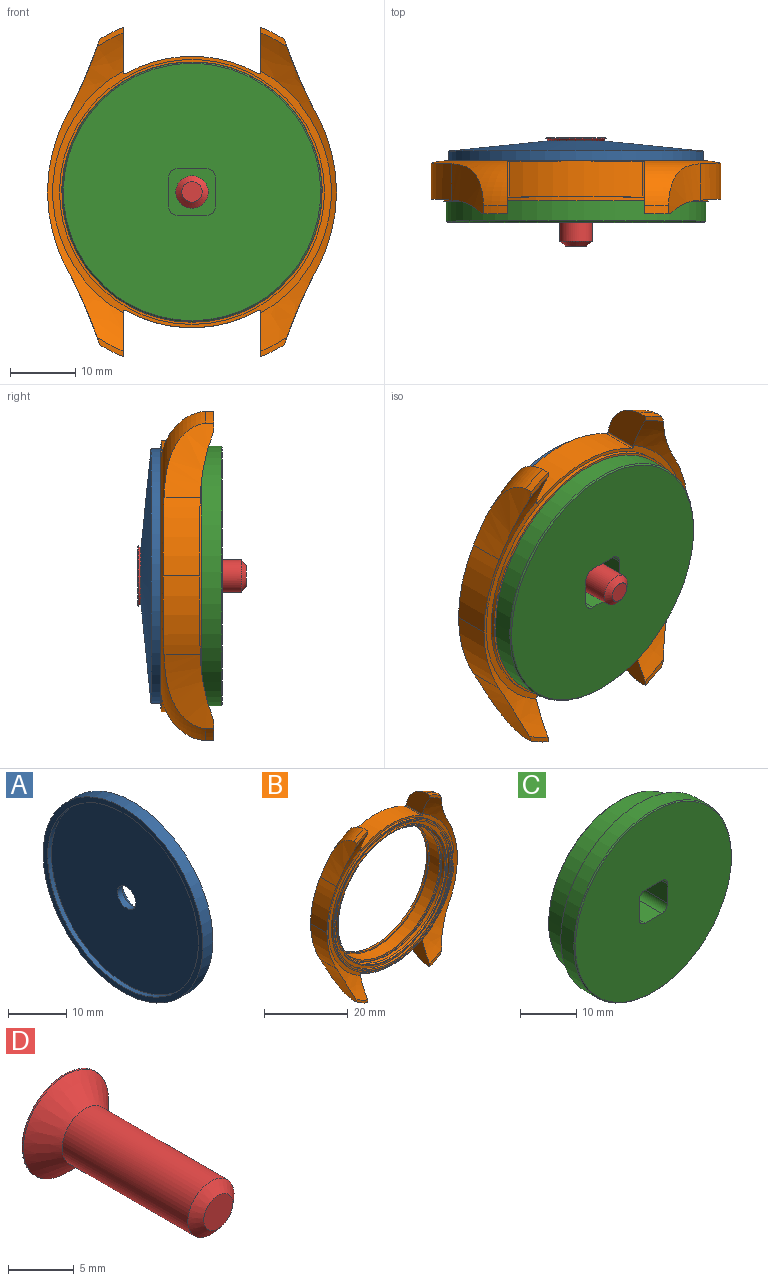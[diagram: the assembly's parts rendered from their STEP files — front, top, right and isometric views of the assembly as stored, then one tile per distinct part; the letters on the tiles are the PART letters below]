
ASSEMBLY  parts=4 mates=3
PART A: 7 faces, bbox 4x38.9x38.9 mm
  f0: cone r=19.47mm half-angle=84.2deg, axis (-1,0,0), area 1141.1mm2, adj f1,f6
  f1: cylinder r=19.47mm len=38.95mm, axis (-1,0,0), area 297.3mm2, adj f0,f2
  f2: plane 38.95x38.95mm, normal (-1,0,0), area 130.5mm2, adj f1,f3
  f3: cylinder r=18.38mm len=36.75mm, axis (-1,0,0), area 107.4mm2, adj f2,f4
  f4: plane 36.75x36.75mm, normal (-1,0,0), area 1044.8mm2, adj f3,f5
  f5: cylinder r=2.25mm len=4.5mm, axis (-1,0,0), area 17.6mm2, adj f4,f6
  f6: bspline ~8.47x8.47mm, area 54.6mm2, adj f0,f5
PART B: 54 faces, bbox 59.5x8.5x59.5 mm
  f0: cylinder r=27.3mm len=3.62mm, axis (0,-1,0), area 5mm2, adj f6,f9,f38,f49
  f1: cylinder r=27.3mm len=3.62mm, axis (0,-1,0), area 5mm2, adj f9,f35,f41,f45
  f2: plane 4x2.97mm, normal (0,-1,0), area 3.3mm2, adj f5,f7,f39,f48
  f3: plane 4x2.97mm, normal (0,-1,0), area 3.3mm2, adj f8,f34,f36,f44
  f4: plane 42.6x41.5mm, normal (0,-1,0), area 113mm2, adj f5,f33,f34,f36,f37,f38,f39,f40
  f5: torus R=10.97mm, axis (0,-1,0), area 112mm2, adj f2,f4,f6,f38,f39,f46,f47,f48
  f6: plane 4x2.97mm, normal (0,-1,0), area 3.3mm2, adj f0,f5,f38,f49
  f7: cylinder r=27.3mm len=3.62mm, axis (0,-1,0), area 5mm2, adj f2,f9,f39,f48
  f8: cylinder r=27.3mm len=3.62mm, axis (0,-1,0), area 5mm2, adj f3,f9,f36,f44
  f9: torus R=19.83mm, axis (0,-1,0), area 415.4mm2, adj f0,f1,f7,f8,f10,f36,f37,f38
  f10: plane 40.38x40.38mm, normal (0,1,0), area 90.5mm2, adj f9,f11
  f11: cylinder r=19.46mm len=38.93mm, axis (0,-1,0), area 137.6mm2, adj f10,f12
  f12: plane 38.93x38.93mm, normal (0,1,0), area 92.9mm2, adj f11,f13
  f13: cylinder r=18.69mm len=37.38mm, axis (0,-1,0), area 23.5mm2, adj f12,f14
  f14: plane 37.38x37.38mm, normal (0,1,0), area 49.2mm2, adj f13,f15
  f15: cone r=18.35mm half-angle=30deg, axis (0,1,0), area 19.9mm2, adj f14,f16
  f16: cylinder r=18.35mm len=36.7mm, axis (0,-1,0), area 89.4mm2, adj f15,f17
  f17: plane 36.7x36.7mm, normal (0,1,0), area 94.9mm2, adj f16,f18
  f18: cylinder r=17.51mm len=35.02mm, axis (0,-1,0), area 66mm2, adj f17,f19
  f19: plane 35.72x35.72mm, normal (0,-1,0), area 38.9mm2, adj f18,f20
  f20: cylinder r=17.86mm len=35.72mm, axis (0,-1,0), area 387.1mm2, adj f19,f21
  f21: plane 36.6x36.6mm, normal (0,-1,0), area 50.3mm2, adj f20,f22
  f22: cylinder r=18.3mm len=36.6mm, axis (0,-1,0), area 34.5mm2, adj f21,f23
  f23: cone r=18.3mm half-angle=43.3deg, axis (0,1,0), area 47.9mm2, adj f22,f24
  f24: cylinder r=18.01mm len=36.03mm, axis (0,-1,0), area 100.6mm2, adj f23,f25
  f25: cone r=18.3mm half-angle=43.3deg, axis (0,-1,0), area 47.9mm2, adj f24,f26
  f26: plane 37.03x37.03mm, normal (0,-1,0), area 24.6mm2, adj f25,f27
  f27: cylinder r=18.51mm len=37.03mm, axis (0,-1,0), area 65.7mm2, adj f26,f28
  f28: plane 39x39mm, normal (0,-1,0), area 117.6mm2, adj f27,f29
  f29: cylinder r=19.5mm len=39mm, axis (0,-1,0), area 75.3mm2, adj f28,f30
  f30: plane 39.83x39.83mm, normal (0,-1,0), area 51.4mm2, adj f29,f31
  f31: cylinder r=19.91mm len=39.83mm, axis (0,-1,0), area 31.3mm2, adj f30,f32
  f32: plane 40.5x40.5mm, normal (0,-1,0), area 42.6mm2, adj f31,f33
  f33: cylinder r=20.25mm len=40.5mm, axis (0,-1,0), area 76.3mm2, adj f4,f32
  f34: torus R=10.97mm, axis (0,-1,0), area 112mm2, adj f3,f4,f35,f36,f41,f42,f43,f44
  f35: plane 4x2.97mm, normal (0,-1,0), area 3.3mm2, adj f1,f34,f41,f45
  f36: plane 8.38x7.32mm, normal (-1,0,0), area 34.6mm2, adj f3,f4,f8,f9,f34,f50
  f37: cylinder r=20.75mm len=20.4mm, axis (0,1,0), area 117.4mm2, adj f4,f9,f50,f51
  f38: plane 8.38x7.32mm, normal (1,0,0), area 34.6mm2, adj f0,f4,f5,f6,f9,f51
  f39: plane 8.38x7.32mm, normal (1,0,0), area 34.6mm2, adj f2,f4,f5,f7,f9,f53
  f40: cylinder r=20.75mm len=20.4mm, axis (0,1,0), area 117.4mm2, adj f4,f9,f52,f53
  f41: plane 8.38x7.32mm, normal (-1,0,0), area 34.6mm2, adj f1,f4,f9,f34,f35,f52
  f42: cylinder r=25.39mm len=12.04mm, axis (0,1,0), area 69.5mm2, adj f9,f34,f43,f45
  f43: cylinder r=25.39mm len=12.04mm, axis (0,1,0), area 69.5mm2, adj f9,f34,f42,f44
  f44: cylinder r=67.35mm len=11.33mm, axis (0,1,0), area 62.4mm2, adj f3,f8,f9,f34,f43
  f45: cylinder r=67.35mm len=11.33mm, axis (0,1,0), area 62.4mm2, adj f1,f9,f34,f35,f42
  f46: cylinder r=25.39mm len=12.04mm, axis (0,1,0), area 69.5mm2, adj f5,f9,f47,f49
  f47: cylinder r=25.39mm len=12.04mm, axis (0,1,0), area 69.5mm2, adj f5,f9,f46,f48
  f48: cylinder r=67.35mm len=11.33mm, axis (0,1,0), area 62.4mm2, adj f2,f5,f7,f9,f47
  f49: cylinder r=67.35mm len=11.33mm, axis (0,1,0), area 62.4mm2, adj f0,f5,f6,f9,f46
  f50: cylinder r=0.2mm len=5.5mm, axis (0,1,0), area 2.3mm2, adj f4,f9,f36,f37
  f51: cylinder r=0.2mm len=5.5mm, axis (0,1,0), area 2.3mm2, adj f4,f9,f37,f38
  f52: cylinder r=0.2mm len=5.5mm, axis (0,1,0), area 2.3mm2, adj f4,f9,f40,f41
  f53: cylinder r=0.2mm len=5.5mm, axis (0,1,0), area 2.3mm2, adj f4,f9,f39,f40
PART C: 17 faces, bbox 39.8x8.8x39.8 mm
  f0: plane 39.35x39.35mm, normal (0,-1,0), area 1166.2mm2, adj f6,f7,f8,f9,f10,f11,f12,f13
  f1: cylinder r=2.25mm len=4.5mm, axis (0,1,0), area 25.4mm2, adj f4,f14
  f2: plane 39.75x39.75mm, normal (0,1,0), area 242.8mm2, adj f3,f5
  f3: cylinder r=17.82mm len=35.65mm, axis (0,-1,0), area 571.2mm2, adj f2,f15
  f4: plane 35.25x35.25mm, normal (0,1,0), area 960mm2, adj f1,f15
  f5: cylinder r=19.88mm len=39.75mm, axis (0,-1,0), area 412.1mm2, adj f2,f16
  f6: plane 7x4.2mm, normal (0,0,1), area 29.4mm2, adj f0,f7,f13,f14
  f7: cylinder r=1.5mm len=7mm, axis (0,-1,0), area 16.5mm2, adj f0,f6,f8,f14
  f8: plane 7x4.2mm, normal (-1,0,0), area 29.4mm2, adj f0,f7,f9,f14
  f9: cylinder r=1.5mm len=7mm, axis (0,-1,0), area 16.5mm2, adj f0,f8,f10,f14
  f10: plane 7x4.2mm, normal (0,0,-1), area 29.4mm2, adj f0,f9,f11,f14
  f11: cylinder r=1.5mm len=7mm, axis (0,-1,0), area 16.5mm2, adj f0,f10,f12,f14
  f12: plane 7x4.2mm, normal (1,0,0), area 29.4mm2, adj f0,f11,f13,f14
  f13: cylinder r=1.5mm len=7mm, axis (0,-1,0), area 16.5mm2, adj f0,f6,f12,f14
  f14: plane 7.2x7.2mm, normal (0,-1,0), area 34mm2, adj f1,f6,f7,f8,f9,f10,f11,f12
  f15: cone r=17.82mm half-angle=45deg, axis (0,-1,0), area 31.5mm2, adj f3,f4
  f16: cone r=19.68mm half-angle=45deg, axis (0,1,0), area 35.1mm2, adj f0,f5
PART D: 19 faces, bbox 10x16.6x10 mm
  f0: cone r=2.49mm half-angle=45deg, axis (0,1,0), area 65.7mm2, adj f2,f3
  f1: plane 9.02x9.02mm, normal (0,1,0), area 58.5mm2, adj f2,f6,f7,f8,f9,f10,f11,f13
  f2: torus R=4.51mm, axis (0,-1,0), area 6.8mm2, adj f0,f1
  f3: cylinder r=2.49mm len=13.54mm, axis (0,-1,0), area 211.7mm2, adj f0,f5
  f4: plane 3.11x3.11mm, normal (0,-1,0), area 7.6mm2, adj f5
  f5: cone r=2.49mm half-angle=50deg, axis (0,1,0), area 15.5mm2, adj f3,f4
  f6: plane 1.5x1.21mm, normal (0.01,0,1), area 1.8mm2, adj f1,f12,f13,f18
  f7: plane 1.5x1.05mm, normal (0.87,0,0.49), area 1.8mm2, adj f1,f12,f13,f14
  f8: plane 1.5x1.05mm, normal (0.86,0,-0.51), area 1.8mm2, adj f1,f12,f14,f15
  f9: plane 1.5x1.21mm, normal (-0.01,0,-1), area 1.8mm2, adj f1,f12,f15,f16
  f10: plane 1.5x1.05mm, normal (-0.87,0,-0.49), area 1.8mm2, adj f1,f12,f16,f17
  f11: plane 1.5x1.05mm, normal (-0.86,0,0.51), area 1.8mm2, adj f1,f12,f17,f18
  f12: plane 2.83x2.51mm, normal (0,1,0), area 5.4mm2, adj f6,f7,f8,f9,f10,f11,f13,f14
  f13: cylinder r=0.2mm len=1.5mm, axis (0,-1,0), area 0.3mm2, adj f1,f6,f7,f12
  f14: cylinder r=0.2mm len=1.5mm, axis (0,-1,0), area 0.3mm2, adj f1,f7,f8,f12
  f15: cylinder r=0.2mm len=1.5mm, axis (0,-1,0), area 0.3mm2, adj f1,f8,f9,f12
  f16: cylinder r=0.2mm len=1.5mm, axis (0,-1,0), area 0.3mm2, adj f1,f9,f10,f12
  f17: cylinder r=0.2mm len=1.5mm, axis (0,-1,0), area 0.3mm2, adj f1,f10,f11,f12
  f18: cylinder r=0.2mm len=1.5mm, axis (0,-1,0), area 0.3mm2, adj f1,f6,f11,f12
PLACE A rot(axis=(0,0,1),90deg) t=(-18.49,-8.27,-2.25)mm
PLACE B t=(-0.93,-13.29,-2.25)mm
PLACE C t=(-18.44,-13.04,-2.25)mm fixed
PLACE D rot(axis=(1,0,0),0deg) t=(-24.44,-20.87,-2.25)mm
MATE fastened A.f0 <-> D.f0  axis (0,-1,0) through (-18.44,-5.64,-2.25)mm
MATE fastened C.f3 <-> B.f0  axis (0,1,0) through (-18.44,-7.74,-2.25)mm
MATE fastened B.f0 <-> A.f0  axis (0,1,0) through (-18.44,-8.07,-2.25)mm
